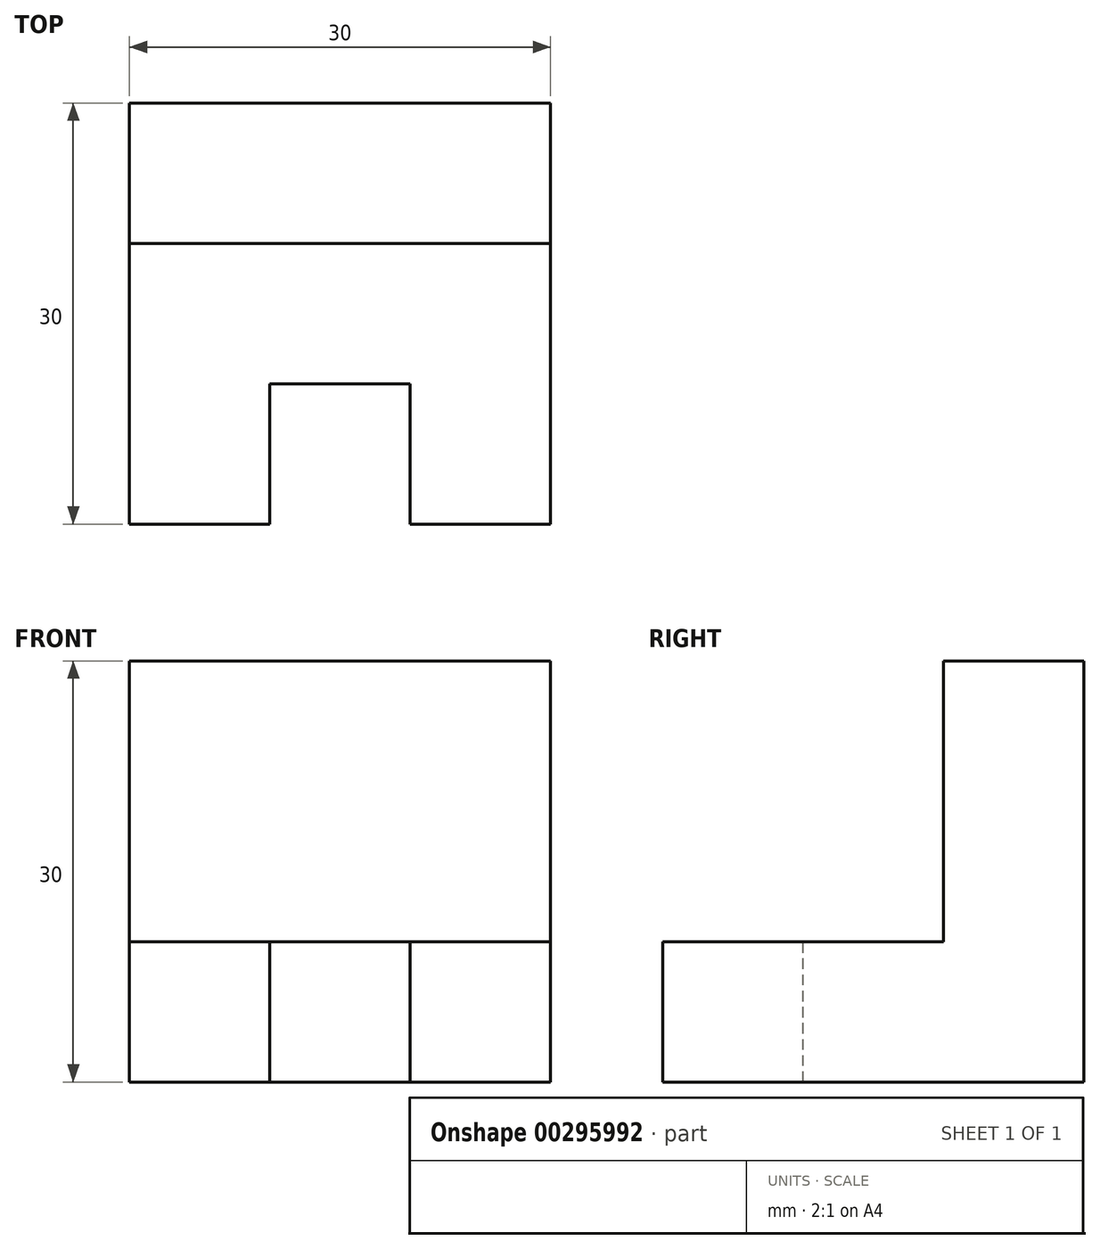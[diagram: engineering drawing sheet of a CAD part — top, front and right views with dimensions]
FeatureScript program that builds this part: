
annotation { "Feature Type Name" : "Feature", "Feature Type Description" : "" }
export const myFeature = defineFeature(function(context is Context, id is Id, definition is map)
    precondition{}
    {
        {
            var Q0;
            Q0=qCreatedBy(makeId("Front.planeOp"),FACE);
            var sketch = newSketch(context, id + "F0", { "sketchPlane" : qUnion([Q0])});
            skLineSegment(sketch, "E0", {"start": v(0, 0) * mm, "end": v(40, 0) * mm});
            skLineSegment(sketch, "E1", {"start": v(40, 0) * mm, "end": v(62.98, 19.28) * mm});
            skLineSegment(sketch, "E2", {"start": v(62.98, 19.28) * mm, "end": v(85.96, 0) * mm});
            skLineSegment(sketch, "E3", {"start": v(40, 0) * mm, "end": v(54.75, 0) * mm, "construction": true});
            skLineSegment(sketch, "E4", {"start": v(85.96, 0) * mm, "end": v(100.96, 0) * mm});
            skLineSegment(sketch, "E5", {"start": v(100.96, 0) * mm, "end": v(100.96, 30) * mm});
            skLineSegment(sketch, "E6", {"start": v(115.96, 30) * mm, "end": v(115.96, 40) * mm});
            skLineSegment(sketch, "E7", {"start": v(115.96, 40) * mm, "end": v(76, 40) * mm});
            skLineSegment(sketch, "E8", {"start": v(100.96, 30) * mm, "end": v(115.96, 30) * mm});
            skLineSegment(sketch, "E9", {"start": v(85.96, 0) * mm, "end": v(54.75, 0) * mm, "construction": true});
            skLineSegment(sketch, "E10", {"start": v(76, 40) * mm, "end": v(51.64, 19.56) * mm});
            skLineSegment(sketch, "E11", {"start": v(51.64, 19.56) * mm, "end": v(51.64, 34.56) * mm});
            skLineSegment(sketch, "E12", {"start": v(51.64, 34.56) * mm, "end": v(44.14, 34.56) * mm});
            skLineSegment(sketch, "E13", {"start": v(44.14, 34.56) * mm, "end": v(44.14, 49.56) * mm});
            skLineSegment(sketch, "E14", {"start": v(44.14, 49.56) * mm, "end": v(14.14, 49.56) * mm});
            skLineSegment(sketch, "E15", {"start": v(14.14, 49.56) * mm, "end": v(0, 35.42) * mm});
            skLineSegment(sketch, "E16", {"start": v(0, 35.42) * mm, "end": v(0, 0) * mm});
            skSolve(sketch);
        }
        {
            var Q0;
            Q0=qCreatedBy(makeId("Top.planeOp"),FACE);
            var sketch = newSketch(context, id + "F1", { "sketchPlane" : qUnion([Q0])});
            skLineSegment(sketch, "E17.bottom", {"start": v(0, 0) * mm, "end": v(30, 0) * mm});
            skLineSegment(sketch, "E17.top", {"start": v(0, 30) * mm, "end": v(30, 30) * mm});
            skLineSegment(sketch, "E17.left", {"start": v(0, 0) * mm, "end": v(0, 30) * mm});
            skLineSegment(sketch, "E17.right", {"start": v(30, 0) * mm, "end": v(30, 30) * mm});
            skSolve(sketch);
        }
        {
            var Q0;
            Q0 = qSketchRegion(id + "F1", true);
            extrude(context, id + "F2", {"entities" : qUnion([Q0]), "depth" : 30 * mm});
        }
        {
            var Q0;
            Q0=makeQuery(id+"F2.opExtrude","CAP_FACE",FACE,{"disambiguationData":[OSD([sQuery(id+"F1.wireOp",EDGE,"E17.bottom"),sQuery(id+"F1.wireOp",EDGE,"E17.top"),sQuery(id+"F1.wireOp",EDGE,"E17.left"),sQuery(id+"F1.wireOp",EDGE,"E17.right")])],"isStart":false});
            var sketch = newSketch(context, id + "F3", { "sketchPlane" : qUnion([Q0])});
            skLineSegment(sketch, "E18.bottom", {"start": v(0, 0) * mm, "end": v(30, 0) * mm});
            skLineSegment(sketch, "E18.top", {"start": v(0, 20) * mm, "end": v(30, 20) * mm});
            skLineSegment(sketch, "E18.left", {"start": v(0, 0) * mm, "end": v(0, 20) * mm});
            skLineSegment(sketch, "E18.right", {"start": v(30, 0) * mm, "end": v(30, 20) * mm});
            skSolve(sketch);
        }
        {
            var Q0;
            Q0=makeQuery(id+"F3.imprint","IMPRINT",FACE,{"disambiguationData":[TD([[makeQuery(id+"F3.imprint","IMPRINT",EDGE,{"derivedFrom":sQuery(id+"F3.wireOp",EDGE,"E18.bottom")}),1.0]])]});
            extrude(context, id + "F4", {"entities" : qUnion([Q0]), "operationType" : NewBodyOperationType.REMOVE, "oppositeDirection" : true, "depth" : 20 * mm});
        }
        {
            var Q0;
            Q0=makeQuery(id+"F4.boolean.opBoolean","COPY",FACE,{"derivedFrom":makeQuery(id+"F4.opExtrude","CAP_FACE",FACE,{"disambiguationData":[OSD([sQuery(id+"F3.wireOp",EDGE,"E18.bottom"),sQuery(id+"F3.wireOp",EDGE,"E18.top"),sQuery(id+"F3.wireOp",EDGE,"E18.left"),sQuery(id+"F3.wireOp",EDGE,"E18.right")])],"isStart":false})});
            var sketch = newSketch(context, id + "F5", { "sketchPlane" : qUnion([Q0])});
            skLineSegment(sketch, "E19", {"start": v(0, 0) * mm, "end": v(10, 0) * mm, "construction": true});
            skLineSegment(sketch, "E20.bottom", {"start": v(10, 0) * mm, "end": v(20, 0) * mm});
            skLineSegment(sketch, "E20.top", {"start": v(10, 10) * mm, "end": v(20, 10) * mm});
            skLineSegment(sketch, "E20.left", {"start": v(10, 0) * mm, "end": v(10, 10) * mm});
            skLineSegment(sketch, "E20.right", {"start": v(20, 0) * mm, "end": v(20, 10) * mm});
            skSolve(sketch);
        }
        {
            var Q0;
            Q0=makeQuery(id+"F5.imprint","IMPRINT",FACE,{"disambiguationData":[TD([[makeQuery(id+"F5.imprint","IMPRINT",EDGE,{"derivedFrom":sQuery(id+"F5.wireOp",EDGE,"E20.bottom")}),1.0]])]});
            extrude(context, id + "F6", {"entities" : qUnion([Q0]), "operationType" : NewBodyOperationType.REMOVE, "oppositeDirection" : true, "depth" : 10 * mm});
        }
    });
